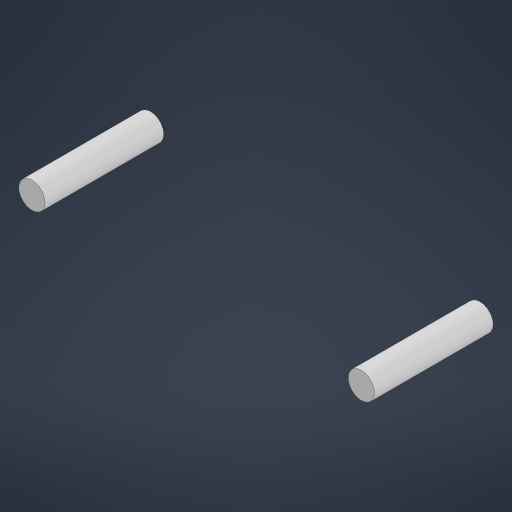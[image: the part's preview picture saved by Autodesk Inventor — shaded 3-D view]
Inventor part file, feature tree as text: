
AUTODESK INVENTOR PART (.ipt)
format: ipt  version: 2024 (Build 280153000, 153)  size: 178,688 bytes
history: native  units: mm
features: other x5, plane x1, extrude x1, sketch x1
ambient origin geometry x8: Origin, YZ Plane, XZ Plane, XY Plane, X Axis, Y Axis, Z Axis, Center Point
bodies: Body1 (feature_tree)
feature tree (8):
  other  "Sólido1"
  plane  "Plano de trabajo1"
  extrude  "Extrusión1"  Depth=18.0mm
  sketch  "Boceto1"  dims[d2=5.0mm d3=5.0mm d4=124.2mm d5=50.0mm d6=18.0mm d7=0.0mm]
  other  "<userpath>\Downloads\Piezas CMR\Marco_APM_002\Marco_apm_002-2.iam"
  other  "Marco_apm_002-2.iam"
  other  "Marco_Conveyor_Aereo:1"
  other  "Marco:1"
